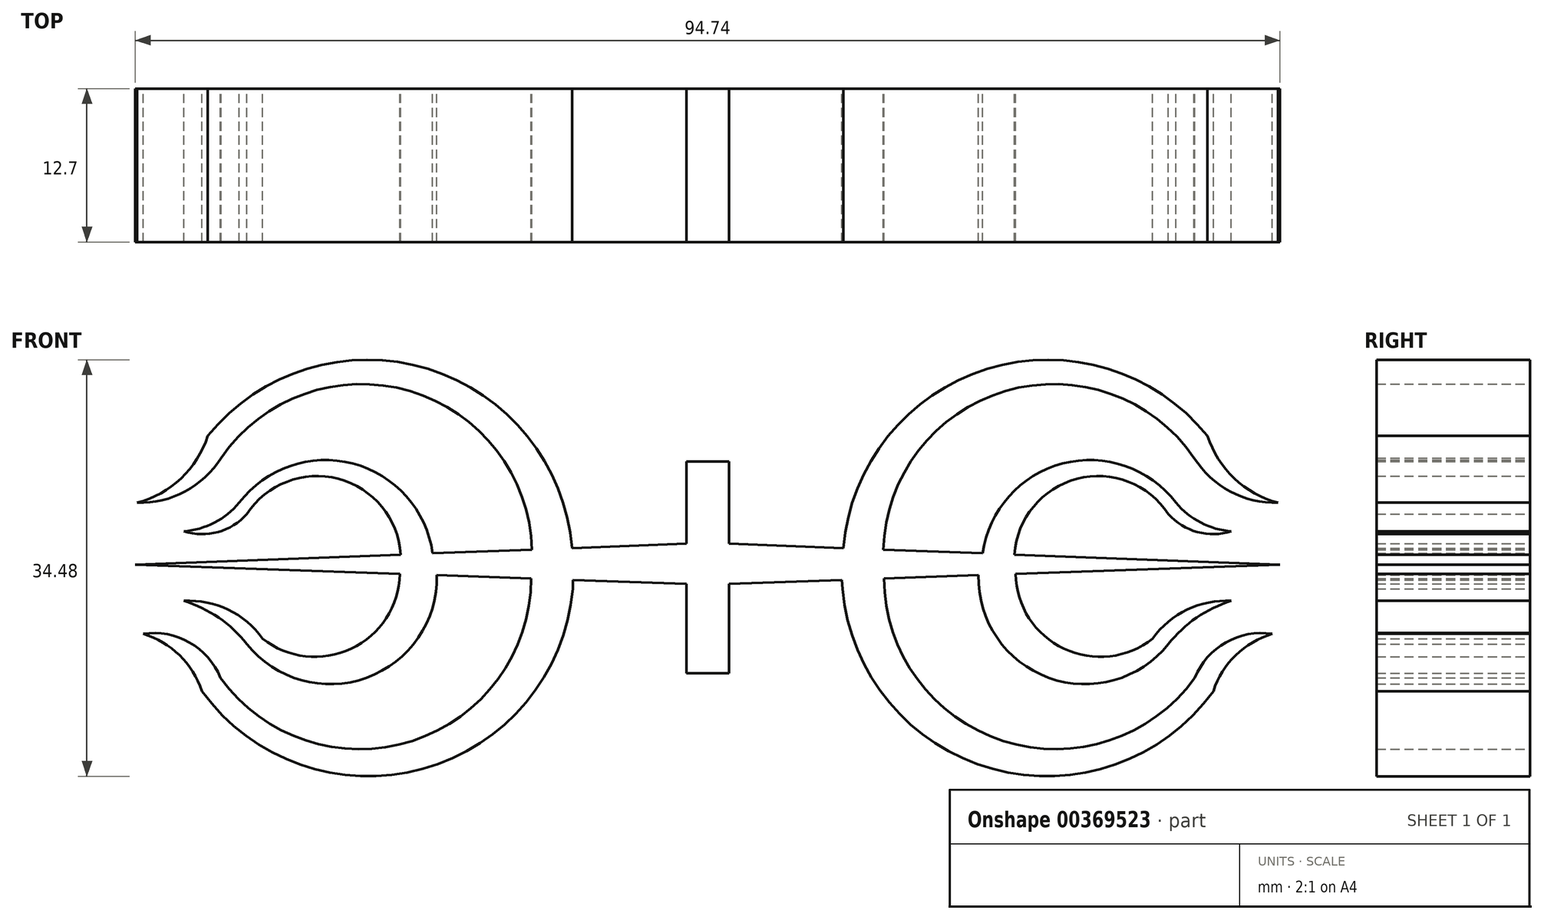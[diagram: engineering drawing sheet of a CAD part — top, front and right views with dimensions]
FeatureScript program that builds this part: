
annotation { "Feature Type Name" : "Feature", "Feature Type Description" : "" }
export const myFeature = defineFeature(function(context is Context, id is Id, definition is map)
    precondition{}
    {
        {
            var Q0;
            Q0=qCreatedBy(makeId("Front.planeOp"),FACE);
            var sketch = newSketch(context, id + "F0", { "sketchPlane" : qUnion([Q0])});
            skArc(sketch, "E0", {"start": v(-14.53, 1.66) * mm, "mid": v(-24.45, 15.14) * mm, "end": v(-40.27, 9.66) * mm});
            skArc(sketch, "E1", {"start": v(-11.19, 1.66) * mm, "mid": v(-22.9, 16.96) * mm, "end": v(-41.37, 11.48) * mm});
            skArc(sketch, "E2", {"start": v(-47.2, 5.96) * mm, "mid": v(-43.24, 6.89) * mm, "end": v(-40.27, 9.66) * mm});
            skArc(sketch, "E3", {"start": v(-47.2, 5.96) * mm, "mid": v(-43.58, 7.97) * mm, "end": v(-41.37, 11.48) * mm});
            skArc(sketch, "E4", {"start": v(-22.75, 1.66) * mm, "mid": v(-29.32, 9.18) * mm, "end": v(-38.77, 5.96) * mm});
            skArc(sketch, "E5", {"start": v(-25.4, 1.66) * mm, "mid": v(-30.56, 7.93) * mm, "end": v(-38.14, 5) * mm});
            skArc(sketch, "E6", {"start": v(-43.34, 3.59) * mm, "mid": v(-40.81, 4.3) * mm, "end": v(-38.77, 5.96) * mm});
            skArc(sketch, "E7", {"start": v(-43.34, 3.59) * mm, "mid": v(-40.53, 3.53) * mm, "end": v(-38.14, 5) * mm});
            skArc(sketch, "E8", {"start": v(-38.14, -5.75) * mm, "mid": v(-28.23, -8.54) * mm, "end": v(-22.41, -0.04) * mm});
            skArc(sketch, "E9", {"start": v(-36.83, -5.3) * mm, "mid": v(-29.5, -6.13) * mm, "end": v(-25.48, 0.06) * mm});
            skArc(sketch, "E10", {"start": v(-36.83, -5.3) * mm, "mid": v(-39.69, -2.9) * mm, "end": v(-43.34, -2.17) * mm});
            skArc(sketch, "E11", {"start": v(-38.14, -5.75) * mm, "mid": v(-40.47, -3.56) * mm, "end": v(-43.34, -2.17) * mm});
            skArc(sketch, "E12", {"start": v(-40.32, -8.55) * mm, "mid": v(-24.47, -13.77) * mm, "end": v(-14.6, -0.32) * mm});
            skArc(sketch, "E13", {"start": v(-40.32, -8.55) * mm, "mid": v(-42.89, -5.6) * mm, "end": v(-46.73, -4.9) * mm});
            skLineSegment(sketch, "E14", {"start": v(-1.76, 2.56) * mm, "end": v(-47.37, 0.83) * mm});
            skLineSegment(sketch, "E15", {"start": v(-47.37, 0.83) * mm, "end": v(-1.76, -0.77) * mm});
            skLineSegment(sketch, "E16", {"start": v(-1.76, -0.77) * mm, "end": v(-47.37, 0.83) * mm});
            skArc(sketch, "E17.MirrorCS", {"start": v(11.19, 1.66) * mm, "mid": v(22.9, 16.96) * mm, "end": v(41.37, 11.48) * mm});
            skArc(sketch, "E18.MirrorCS", {"start": v(14.53, 1.66) * mm, "mid": v(24.45, 15.14) * mm, "end": v(40.27, 9.66) * mm});
            skArc(sketch, "E19.MirrorCS", {"start": v(47.2, 5.96) * mm, "mid": v(43.58, 7.97) * mm, "end": v(41.37, 11.48) * mm});
            skArc(sketch, "E20.MirrorCS", {"start": v(47.2, 5.96) * mm, "mid": v(43.24, 6.89) * mm, "end": v(40.27, 9.66) * mm});
            skArc(sketch, "E21.MirrorCS", {"start": v(22.75, 1.66) * mm, "mid": v(29.32, 9.18) * mm, "end": v(38.77, 5.96) * mm});
            skArc(sketch, "E22.MirrorCS", {"start": v(25.4, 1.66) * mm, "mid": v(30.56, 7.93) * mm, "end": v(38.14, 5) * mm});
            skArc(sketch, "E23.MirrorCS", {"start": v(36.83, -5.3) * mm, "mid": v(29.5, -6.13) * mm, "end": v(25.48, 0.06) * mm});
            skArc(sketch, "E24.MirrorCS", {"start": v(38.14, -5.75) * mm, "mid": v(28.23, -8.54) * mm, "end": v(22.41, -0.04) * mm});
            skArc(sketch, "E25.MirrorCS", {"start": v(43.34, 3.59) * mm, "mid": v(40.53, 3.53) * mm, "end": v(38.14, 5) * mm});
            skArc(sketch, "E26.MirrorCS", {"start": v(43.34, 3.59) * mm, "mid": v(40.81, 4.3) * mm, "end": v(38.77, 5.96) * mm});
            skArc(sketch, "E27.MirrorCS", {"start": v(36.83, -5.3) * mm, "mid": v(39.69, -2.9) * mm, "end": v(43.34, -2.17) * mm});
            skArc(sketch, "E28.MirrorCS", {"start": v(38.14, -5.75) * mm, "mid": v(40.47, -3.56) * mm, "end": v(43.34, -2.17) * mm});
            skArc(sketch, "E29.MirrorCS", {"start": v(40.32, -8.55) * mm, "mid": v(24.47, -13.77) * mm, "end": v(14.6, -0.32) * mm});
            skArc(sketch, "E30.MirrorCS", {"start": v(40.32, -8.55) * mm, "mid": v(42.89, -5.6) * mm, "end": v(46.73, -4.9) * mm});
            skLineSegment(sketch, "E31.MirrorCS", {"start": v(1.76, 2.56) * mm, "end": v(47.37, 0.83) * mm});
            skLineSegment(sketch, "E32.MirrorCS", {"start": v(1.76, -0.77) * mm, "end": v(47.37, 0.83) * mm});
            skLineSegment(sketch, "E33", {"start": v(-1.76, 2.56) * mm, "end": v(-1.76, 9.35) * mm});
            skLineSegment(sketch, "E34", {"start": v(-1.76, 9.35) * mm, "end": v(1.76, 9.35) * mm});
            skLineSegment(sketch, "E35", {"start": v(1.76, 9.35) * mm, "end": v(1.76, 2.56) * mm});
            skLineSegment(sketch, "E36", {"start": v(1.76, -0.77) * mm, "end": v(1.76, -8.16) * mm});
            skLineSegment(sketch, "E37", {"start": v(1.76, -8.16) * mm, "end": v(-1.76, -8.16) * mm});
            skLineSegment(sketch, "E38", {"start": v(-1.76, -8.16) * mm, "end": v(-1.76, -0.77) * mm});
            skArc(sketch, "E39", {"start": v(-41.86, -9.64) * mm, "mid": v(-23.57, -16.08) * mm, "end": v(-11.16, -1.18) * mm});
            skArc(sketch, "E40", {"start": v(-41.86, -9.64) * mm, "mid": v(-43.71, -6.67) * mm, "end": v(-46.73, -4.9) * mm});
            skArc(sketch, "E41.MirrorCS", {"start": v(41.86, -9.64) * mm, "mid": v(23.57, -16.08) * mm, "end": v(11.16, -1.18) * mm});
            skArc(sketch, "E42.MirrorCS", {"start": v(41.86, -9.64) * mm, "mid": v(43.71, -6.67) * mm, "end": v(46.73, -4.9) * mm});
            skLineSegment(sketch, "E43", {"start": v(-11.16, -1.18) * mm, "end": v(-11.16, -0.44) * mm});
            skLineSegment(sketch, "E44", {"start": v(-11.16, -0.44) * mm, "end": v(-11.16, -1.18) * mm});
            skLineSegment(sketch, "E45", {"start": v(11.16, -1.18) * mm, "end": v(11.1, -0.44) * mm});
            skLineSegment(sketch, "E46", {"start": v(11.1, -0.44) * mm, "end": v(11.16, -1.18) * mm});
            skSolve(sketch);
        }
        {
            var Q0;
            Q0=qSketchRegion(id+"F0",true);
            extrude(context, id + "F1", {"entities" : qUnion([Q0]), "depth" : 12.7 * mm});
        }
    });
